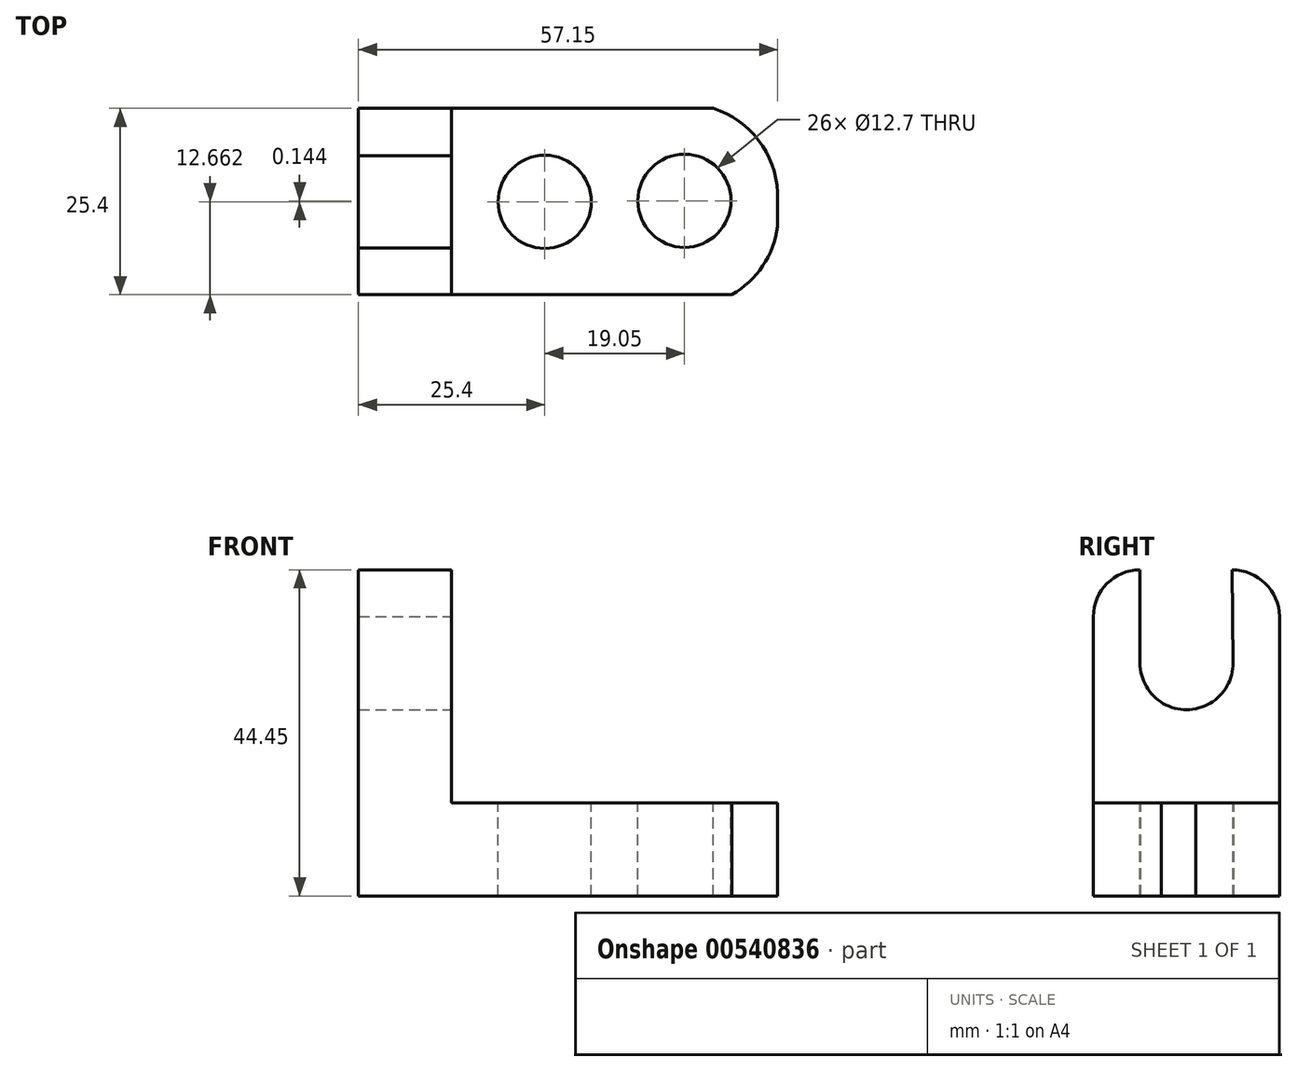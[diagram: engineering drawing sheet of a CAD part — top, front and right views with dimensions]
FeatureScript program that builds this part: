
annotation { "Feature Type Name" : "Feature", "Feature Type Description" : "" }
export const myFeature = defineFeature(function(context is Context, id is Id, definition is map)
    precondition{}
    {
        {
            var Q0;
            Q0=qCreatedBy(makeId("Front.planeOp"),FACE);
            var sketch = newSketch(context, id + "F0", { "sketchPlane" : qUnion([Q0])});
            skLineSegment(sketch, "E0", {"start": v(0, 0) * mm, "end": v(57.15, 0) * mm});
            skLineSegment(sketch, "E1", {"start": v(57.15, 0) * mm, "end": v(57.15, 12.7) * mm});
            skLineSegment(sketch, "E2", {"start": v(57.15, 12.7) * mm, "end": v(12.7, 12.7) * mm});
            skLineSegment(sketch, "E3", {"start": v(12.7, 12.7) * mm, "end": v(12.7, 44.45) * mm});
            skLineSegment(sketch, "E4", {"start": v(12.7, 44.45) * mm, "end": v(0, 44.45) * mm});
            skLineSegment(sketch, "E5", {"start": v(0, 44.45) * mm, "end": v(0, 0) * mm});
            skSolve(sketch);
        }
        {
            var Q0;
            Q0=makeQuery(id+"F0.imprint","IMPRINT",FACE,{"disambiguationData":[TD([[makeQuery(id+"F0.imprint","IMPRINT",EDGE,{"derivedFrom":sQuery(id+"F0.wireOp",EDGE,"E0")}),1.0]])]});
            extrude(context, id + "F1", {"entities" : qUnion([Q0]), "depth" : 25.4 * mm, "offsetDistance" : 25.4 * mm});
        }
        {
            var Q0;
            Q0=makeQuery(id+"F1.opExtrude","SWEPT_FACE",FACE,{"disambiguationData":[OSD([sQuery(id+"F0.wireOp",EDGE,"E3")])]});
            var sketch = newSketch(context, id + "F2", { "sketchPlane" : qUnion([Q0])});
            skCircle(sketch, "E6", {"center": v(-12.7, 31.75) * mm, "radius": 6.35 * mm});
            skPoint(sketch, "E6.centerSnap0", {"position": v(-12.7, 44.45) * mm});
            skLineSegment(sketch, "E7", {"start": v(-12.7, 31.75) * mm, "end": v(-19.05, 31.75) * mm});
            skLineSegment(sketch, "E8", {"start": v(-19.05, 31.75) * mm, "end": v(-19.05, 44.45) * mm});
            skLineSegment(sketch, "E9", {"start": v(-19.05, 44.45) * mm, "end": v(-6.48, 44.45) * mm});
            skLineSegment(sketch, "E10", {"start": v(-6.35, 31.75) * mm, "end": v(-12.7, 31.75) * mm});
            skLineSegment(sketch, "E11", {"start": v(-6.35, 31.75) * mm, "end": v(-6.48, 44.45) * mm});
            skArc(sketch, "E12", {"start": v(-19.05, 44.45) * mm, "mid": v(-23.54, 42.6) * mm, "end": v(-25.4, 38.1) * mm});
            skArc(sketch, "E13", {"start": v(0, 38.1) * mm, "mid": v(-1.94, 42.6) * mm, "end": v(-6.48, 44.45) * mm});
            skSolve(sketch);
        }
        {
            var Q0;
            {var subQ0=sQuery(id+"F2.wireOp",EDGE,"E8");Q0=makeQuery(id+"F2.imprint","IMPRINT",FACE,{"disambiguationData":[TD([[makeQuery(id+"F2.imprint","IMPRINT",EDGE,{"derivedFrom":subQ0}),-1.0]])]});}
            var Q1;
            {var subQ0=sQuery(id+"F2.wireOp",EDGE,"E7");Q1=makeQuery(id+"F2.imprint","IMPRINT",FACE,{"disambiguationData":[TD([[makeQuery(id+"F2.imprint","IMPRINT",EDGE,{"derivedFrom":subQ0}),-1.0]])]});}
            var Q2;
            {var subQ0=sQuery(id+"F2.wireOp",EDGE,"E7");Q2=makeQuery(id+"F2.imprint","IMPRINT",FACE,{"disambiguationData":[TD([[makeQuery(id+"F2.imprint","IMPRINT",EDGE,{"derivedFrom":subQ0}),1.0]])]});}
            var Q3;
            {var subQ0=sQuery(id+"F2.wireOp",EDGE,"E13");Q3=makeQuery(id+"F2.imprint","IMPRINT",FACE,{"disambiguationData":[TD([[makeQuery(id+"F2.imprint","IMPRINT",EDGE,{"derivedFrom":subQ0}),-1.0]])]});}
            var Q4;
            {var subQ0=sQuery(id+"F2.wireOp",EDGE,"E12");Q4=makeQuery(id+"F2.imprint","IMPRINT",FACE,{"disambiguationData":[TD([[makeQuery(id+"F2.imprint","IMPRINT",EDGE,{"derivedFrom":subQ0}),-1.0]])]});}
            extrude(context, id + "F3", {"entities" : qUnion([Q0, Q1, Q2, Q3, Q4]), "operationType" : NewBodyOperationType.REMOVE, "oppositeDirection" : true, "depth" : 12.7 * mm, "offsetDistance" : 25.4 * mm});
        }
        {
            var Q0;
            Q0=makeQuery(id+"F1.opExtrude","SWEPT_FACE",FACE,{"disambiguationData":[OSD([sQuery(id+"F0.wireOp",EDGE,"E2")])]});
            var sketch = newSketch(context, id + "F4", { "sketchPlane" : qUnion([Q0])});
            skCircle(sketch, "E14", {"center": v(25.4, -12.74) * mm, "radius": 6.35 * mm});
            skCircle(sketch, "E15", {"center": v(44.45, -12.6) * mm, "radius": 6.35 * mm});
            skArc(sketch, "E16", {"start": v(57.15, -12.7) * mm, "mid": v(54.92, -4.87) * mm, "end": v(48.4, 0) * mm});
            skArc(sketch, "E17", {"start": v(50.91, -25.4) * mm, "mid": v(55.96, -20) * mm, "end": v(57.15, -12.7) * mm});
            skSolve(sketch);
        }
        {
            var Q0;
            Q0=makeQuery(id+"F4.imprint","IMPRINT",FACE,{"disambiguationData":[TD([[makeQuery(id+"F4.imprint","IMPRINT",EDGE,{"derivedFrom":sQuery(id+"F4.wireOp",EDGE,"E14")}),1.0]])]});
            var Q1;
            Q1=makeQuery(id+"F4.imprint","IMPRINT",FACE,{"disambiguationData":[TD([[makeQuery(id+"F4.imprint","IMPRINT",EDGE,{"derivedFrom":sQuery(id+"F4.wireOp",EDGE,"E15")}),1.0]])]});
            var Q2;
            {var subQ0=sQuery(id+"F4.wireOp",EDGE,"E16");var subQ1=sQuery(id+"F0.wireOp",EDGE,"E2");var subQ2=makeQuery(id+"F1.opExtrude","CAP_EDGE",EDGE,{"disambiguationData":[OSD([subQ1])],"isStart":true});var subQ3=makeQuery(id+"F4.imprint","INTERSECT",VERTEX,{"derivedFrom":[subQ2,subQ0]});Q2=makeQuery(id+"F4.imprint","IMPRINT",FACE,{"disambiguationData":[TD([[makeQuery(id+"F4.imprint","IMPRINT",EDGE,{"disambiguationData":[TD([[subQ3,1.0]])],"derivedFrom":subQ0}),-1.0]])]});}
            var Q3;
            {var subQ0=sQuery(id+"F4.wireOp",EDGE,"E17");var subQ1=sQuery(id+"F0.wireOp",EDGE,"E2");var subQ2=makeQuery(id+"F1.opExtrude","CAP_EDGE",EDGE,{"disambiguationData":[OSD([subQ1])],"isStart":false});var subQ3=makeQuery(id+"F4.imprint","INTERSECT",VERTEX,{"derivedFrom":[subQ2,subQ0]});Q3=makeQuery(id+"F4.imprint","IMPRINT",FACE,{"disambiguationData":[TD([[makeQuery(id+"F4.imprint","IMPRINT",EDGE,{"disambiguationData":[TD([[subQ3,-1.0]])],"derivedFrom":subQ0}),-1.0]])]});}
            extrude(context, id + "F5", {"entities" : qUnion([Q0, Q1, Q2, Q3]), "operationType" : NewBodyOperationType.REMOVE, "oppositeDirection" : true, "depth" : 25.4 * mm, "offsetDistance" : 25.4 * mm});
        }
    });
